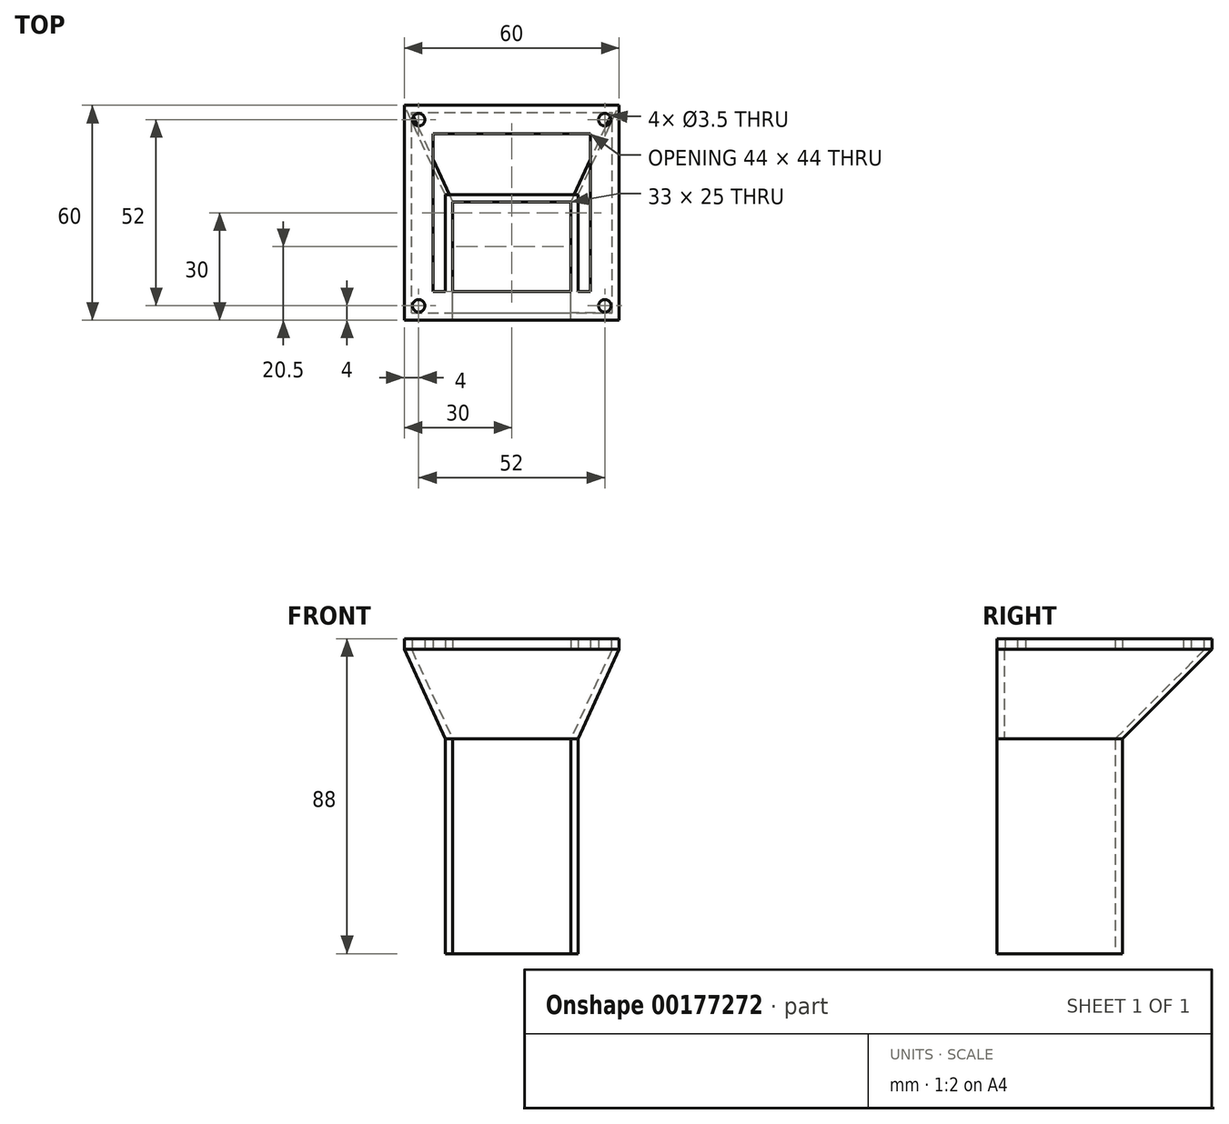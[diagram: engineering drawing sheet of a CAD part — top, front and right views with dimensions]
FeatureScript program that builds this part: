
annotation { "Feature Type Name" : "Feature", "Feature Type Description" : "" }
export const myFeature = defineFeature(function(context is Context, id is Id, definition is map)
    precondition{}
    {
        {
            var Q0;
            Q0=qCreatedBy(makeId("Top.planeOp"),FACE);
            var sketch = newSketch(context, id + "F0", { "sketchPlane" : qUnion([Q0])});
            skLineSegment(sketch, "E0.bottom", {"start": v(0, 0) * mm, "end": v(33, 0) * mm});
            skLineSegment(sketch, "E0.top", {"start": v(0, 33) * mm, "end": v(33, 33) * mm});
            skLineSegment(sketch, "E0.left", {"start": v(0, 0) * mm, "end": v(0, 33) * mm});
            skLineSegment(sketch, "E0.right", {"start": v(33, 0) * mm, "end": v(33, 33) * mm});
            skLineSegment(sketch, "E1.0", {"start": v(-2, 35) * mm, "end": v(35, 35) * mm});
            skLineSegment(sketch, "E1.1", {"start": v(-2, 0) * mm, "end": v(-2, 35) * mm});
            skLineSegment(sketch, "E1.3", {"start": v(35, 0) * mm, "end": v(35, 35) * mm});
            skLineSegment(sketch, "E2", {"start": v(33, 0) * mm, "end": v(35, 0) * mm});
            skLineSegment(sketch, "E3", {"start": v(0, 0) * mm, "end": v(-2, 0) * mm});
            skSolve(sketch);
        }
        {
            var Q0;
            Q0=makeQuery(id+"F0.imprint","IMPRINT",FACE,{"disambiguationData":[TD([[makeQuery(id+"F0.imprint","IMPRINT",EDGE,{"derivedFrom":sQuery(id+"F0.wireOp",EDGE,"E0.top")}),1.0]])]});
            extrude(context, id + "F1", {"entities" : qUnion([Q0]), "depth" : 60 * mm});
        }
        {
            var Q0;
            Q0=makeQuery(id+"F1.opExtrude","CAP_FACE",FACE,{"disambiguationData":[OSD([sQuery(id+"F0.wireOp",EDGE,"E0.top"),sQuery(id+"F0.wireOp",EDGE,"E0.left"),sQuery(id+"F0.wireOp",EDGE,"E0.right"),sQuery(id+"F0.wireOp",EDGE,"E1.0"),sQuery(id+"F0.wireOp",EDGE,"E1.1"),sQuery(id+"F0.wireOp",EDGE,"E1.3"),sQuery(id+"F0.wireOp",EDGE,"E2"),sQuery(id+"F0.wireOp",EDGE,"E3")])],"isStart":false});
            cPlane(context, id + "F2", {"entities" : qUnion([Q0]), "cplaneType" : CPlaneType.OFFSET, "offset" : 25 * mm, "width" : 150 * mm, "height" : 150 * mm});
        }
        {
            var Q0;
            Q0=qCreatedBy(id+"F2.planeOp",FACE);
            var sketch = newSketch(context, id + "F3", { "sketchPlane" : qUnion([Q0])});
            skLineSegment(sketch, "E4.0.0", {"start": v(0, 0) * mm, "end": v(0, 33) * mm});
            skLineSegment(sketch, "E4.0.1", {"start": v(0, 33) * mm, "end": v(33, 33) * mm});
            skLineSegment(sketch, "E4.0.2", {"start": v(33, 33) * mm, "end": v(33, 0) * mm});
            skLineSegment(sketch, "E4.0.3", {"start": v(33, 0) * mm, "end": v(35, 0) * mm});
            skLineSegment(sketch, "E4.0.4", {"start": v(35, 0) * mm, "end": v(35, 35) * mm});
            skLineSegment(sketch, "E4.0.5", {"start": v(35, 35) * mm, "end": v(-2, 35) * mm});
            skLineSegment(sketch, "E4.0.6", {"start": v(-2, 35) * mm, "end": v(-2, 0) * mm});
            skLineSegment(sketch, "E4.0.7", {"start": v(-2, 0) * mm, "end": v(0, 0) * mm});
            skLineSegment(sketch, "E5.bottom", {"start": v(-13.5, 0) * mm, "end": v(46.5, 0) * mm});
            skLineSegment(sketch, "E5.top", {"start": v(-13.5, 60) * mm, "end": v(46.5, 60) * mm});
            skLineSegment(sketch, "E5.left", {"start": v(-13.5, 0) * mm, "end": v(-13.5, 60) * mm});
            skLineSegment(sketch, "E5.right", {"start": v(46.5, 0) * mm, "end": v(46.5, 60) * mm});
            skLineSegment(sketch, "E6", {"start": v(16.5, 60.15) * mm, "end": v(16.5, -12.5) * mm, "construction": true});
            skPoint(sketch, "E6.startSnap0", {"position": v(16.5, 35) * mm});
            skPoint(sketch, "E6.endSnap0", {"position": v(16.5, 35) * mm});
            skLineSegment(sketch, "E7.0", {"start": v(-5.5, 52) * mm, "end": v(38.5, 52) * mm});
            skLineSegment(sketch, "E7.1", {"start": v(-5.5, 8) * mm, "end": v(-5.5, 52) * mm});
            skLineSegment(sketch, "E7.2", {"start": v(-5.5, 8) * mm, "end": v(38.5, 8) * mm});
            skLineSegment(sketch, "E7.3", {"start": v(38.5, 8) * mm, "end": v(38.5, 52) * mm});
            skCircle(sketch, "E8", {"center": v(-9.5, 56) * mm, "radius": 1.75 * mm});
            skCircle(sketch, "E9", {"center": v(-9.5, 4) * mm, "radius": 1.75 * mm});
            skCircle(sketch, "E10", {"center": v(42.5, 4) * mm, "radius": 1.75 * mm});
            skCircle(sketch, "E11", {"center": v(42.5, 56) * mm, "radius": 1.75 * mm});
            skLineSegment(sketch, "E12", {"start": v(-5.5, 8) * mm, "end": v(-5.5, 0) * mm});
            skLineSegment(sketch, "E13", {"start": v(38.5, 8) * mm, "end": v(38.5, 0) * mm});
            skSolve(sketch);
        }
        {
            var Q0;
            Q0=makeQuery(id+"F3.imprint","IMPRINT",FACE,{"disambiguationData":[TD([[makeQuery(id+"F3.imprint","IMPRINT",EDGE,{"derivedFrom":sQuery(id+"F3.wireOp",EDGE,"E5.top")}),-1.0]])]});
            var Q1;
            {var subQ5=sQuery(id+"F3.wireOp",EDGE,"E12");Q1=makeQuery(id+"F3.imprint","IMPRINT",FACE,{"disambiguationData":[TD([[makeQuery(id+"F3.imprint","IMPRINT",EDGE,{"derivedFrom":subQ5}),1.0]])]});}
            var Q2;
            {var subQ5=sQuery(id+"F3.wireOp",EDGE,"E13");Q2=makeQuery(id+"F3.imprint","IMPRINT",FACE,{"disambiguationData":[TD([[makeQuery(id+"F3.imprint","IMPRINT",EDGE,{"derivedFrom":subQ5}),-1.0]])]});}
            var Q3;
            {var subQ0=sQuery(id+"F3.wireOp",EDGE,"E5.bottom");var subQ1=sQuery(id+"F3.wireOp",EDGE,"E4.0.2");var subQ2=makeQuery(id+"F3.imprint","INTERSECT",VERTEX,{"derivedFrom":[subQ1,subQ0]});Q3=makeQuery(id+"F3.imprint","IMPRINT",FACE,{"disambiguationData":[TD([[makeQuery(id+"F3.imprint","IMPRINT",EDGE,{"disambiguationData":[TD([[subQ2,1.0]])],"derivedFrom":subQ1}),1.0]])]});}
            var Q4;
            {var subQ0=sQuery(id+"F3.wireOp",EDGE,"E5.bottom");var subQ1=sQuery(id+"F3.wireOp",EDGE,"E4.0.0");var subQ2=makeQuery(id+"F3.imprint","INTERSECT",VERTEX,{"derivedFrom":[subQ1,subQ0]});Q4=makeQuery(id+"F3.imprint","IMPRINT",FACE,{"disambiguationData":[TD([[makeQuery(id+"F3.imprint","IMPRINT",EDGE,{"disambiguationData":[TD([[subQ2,-1.0]])],"derivedFrom":subQ1}),1.0]])]});}
            var Q5;
            Q5=makeQuery(id+"F3.imprint","IMPRINT",FACE,{"disambiguationData":[TD([[makeQuery(id+"F3.imprint","IMPRINT",EDGE,{"derivedFrom":sQuery(id+"F3.wireOp",EDGE,"E7.0")}),1.0]])]});
            var Q6;
            {var subQ0=sQuery(id+"F3.wireOp",EDGE,"af95f293-ccdd-4cf6-88c4-fea35add42e6.1");var subQ1=sQuery(id+"F3.wireOp",EDGE,"E4.0.0");var subQ2=makeQuery(id+"F3.imprint","INTERSECT",VERTEX,{"derivedFrom":[subQ1,subQ0]});Q6=makeQuery(id+"F3.imprint","IMPRINT",FACE,{"disambiguationData":[TD([[makeQuery(id+"F3.imprint","IMPRINT",EDGE,{"disambiguationData":[TD([[subQ2,-1.0]])],"derivedFrom":subQ1}),1.0]])]});}
            var Q7;
            {var subQ0=sQuery(id+"F3.wireOp",EDGE,"E7.2");var subQ1=sQuery(id+"F3.wireOp",EDGE,"E4.0.2");var subQ2=makeQuery(id+"F3.imprint","INTERSECT",VERTEX,{"derivedFrom":[subQ1,subQ0]});Q7=makeQuery(id+"F3.imprint","IMPRINT",FACE,{"disambiguationData":[TD([[makeQuery(id+"F3.imprint","IMPRINT",EDGE,{"disambiguationData":[TD([[subQ2,-1.0]])],"derivedFrom":subQ1}),1.0]])]});}
            var Q8;
            {var subQ0=sQuery(id+"F3.wireOp",EDGE,"E5.bottom");var subQ1=sQuery(id+"F3.wireOp",EDGE,"E4.0.0");var subQ2=makeQuery(id+"F3.imprint","INTERSECT",VERTEX,{"derivedFrom":[subQ1,subQ0]});Q8=makeQuery(id+"F3.imprint","IMPRINT",FACE,{"disambiguationData":[TD([[makeQuery(id+"F3.imprint","IMPRINT",EDGE,{"disambiguationData":[TD([[subQ2,-1.0]])],"derivedFrom":subQ1}),-1.0]])]});}
            extrude(context, id + "F4", {"entities" : qUnion([Q0, Q1, Q2, Q3, Q4, Q5, Q6, Q7, Q8]), "depth" : 3 * mm});
        }
        {
            var Q0;
            Q0=makeQuery(id+"F3.imprint","IMPRINT",FACE,{"disambiguationData":[TD([[makeQuery(id+"F3.imprint","IMPRINT",EDGE,{"derivedFrom":sQuery(id+"F3.wireOp",EDGE,"E5.top")}),-1.0]])]});
            var sketch = newSketch(context, id + "F5", { "sketchPlane" : qUnion([Q0])});
            skLineSegment(sketch, "E14.0", {"start": v(-13.5, 0) * mm, "end": v(-13.5, 60) * mm});
            skLineSegment(sketch, "E15.0", {"start": v(-13.5, 60) * mm, "end": v(46.5, 60) * mm});
            skLineSegment(sketch, "E16.0", {"start": v(46.5, 0) * mm, "end": v(46.5, 60) * mm});
            skLineSegment(sketch, "E17.0", {"start": v(-13.5, 0) * mm, "end": v(46.5, 0) * mm});
            skSolve(sketch);
        }
        {
            var Q0;
            Q0=makeQuery(id+"F1.opExtrude","CAP_FACE",FACE,{"disambiguationData":[OSD([sQuery(id+"F0.wireOp",EDGE,"E0.top"),sQuery(id+"F0.wireOp",EDGE,"E0.left"),sQuery(id+"F0.wireOp",EDGE,"E0.right"),sQuery(id+"F0.wireOp",EDGE,"E1.0"),sQuery(id+"F0.wireOp",EDGE,"E1.1"),sQuery(id+"F0.wireOp",EDGE,"E1.3"),sQuery(id+"F0.wireOp",EDGE,"E2"),sQuery(id+"F0.wireOp",EDGE,"E3")])],"isStart":false});
            var sketch = newSketch(context, id + "F6", { "sketchPlane" : qUnion([Q0])});
            skLineSegment(sketch, "E18.0", {"start": v(-2, 0) * mm, "end": v(-2, 35) * mm});
            skLineSegment(sketch, "E19.0", {"start": v(-2, 35) * mm, "end": v(35, 35) * mm});
            skLineSegment(sketch, "E20.0", {"start": v(35, 0) * mm, "end": v(35, 35) * mm});
            skLineSegment(sketch, "E21", {"start": v(-2, 0) * mm, "end": v(35, 0) * mm});
            skSolve(sketch);
        }
        {
            var Q0;
            Q0 = qSketchRegion(id + "F6", true);
            var Q1;
            Q1 = qSketchRegion(id + "F5", true);
            loft(context, id + "F7", {"sheetProfilesArray" : [{ "sheetProfileEntities" : qUnion([Q0]) }, { "sheetProfileEntities" : qUnion([Q1]) }]});
        }
        {
            var Q0;
            Q0=makeQuery(id+"F4.opExtrude","CAP_FACE",FACE,{"disambiguationData":[OSD([sQuery(id+"F3.wireOp",EDGE,"E4.0.0"),sQuery(id+"F3.wireOp",EDGE,"E4.0.2"),sQuery(id+"F3.wireOp",EDGE,"E5.top"),sQuery(id+"F3.wireOp",EDGE,"E5.left"),sQuery(id+"F3.wireOp",EDGE,"E5.right"),sQuery(id+"F3.wireOp",EDGE,"E5.bottom"),sQuery(id+"F3.wireOp",EDGE,"E7.0"),sQuery(id+"F3.wireOp",EDGE,"E7.1"),sQuery(id+"F3.wireOp",EDGE,"E7.2"),sQuery(id+"F3.wireOp",EDGE,"E7.3"),sQuery(id+"F3.wireOp",EDGE,"E8"),sQuery(id+"F3.wireOp",EDGE,"E9"),sQuery(id+"F3.wireOp",EDGE,"E10"),sQuery(id+"F3.wireOp",EDGE,"E11")])],"isStart":true});
            cPlane(context, id + "F8", {"entities" : qUnion([Q0]), "cplaneType" : CPlaneType.OFFSET, "offset" : 0 * mm, "width" : 150 * mm, "height" : 150 * mm});
        }
        {
            var Q0;
            Q0=makeQuery(id+"F1.opExtrude","CAP_FACE",FACE,{"disambiguationData":[OSD([sQuery(id+"F0.wireOp",EDGE,"E0.top"),sQuery(id+"F0.wireOp",EDGE,"E0.left"),sQuery(id+"F0.wireOp",EDGE,"E0.right"),sQuery(id+"F0.wireOp",EDGE,"E1.0"),sQuery(id+"F0.wireOp",EDGE,"E1.1"),sQuery(id+"F0.wireOp",EDGE,"E1.3"),sQuery(id+"F0.wireOp",EDGE,"E2"),sQuery(id+"F0.wireOp",EDGE,"E3")])],"isStart":false});
            var sketch = newSketch(context, id + "F9", { "sketchPlane" : qUnion([Q0])});
            skLineSegment(sketch, "E22.0", {"start": v(0, 2) * mm, "end": v(0, 33) * mm});
            skLineSegment(sketch, "E23.0", {"start": v(0, 33) * mm, "end": v(33, 33) * mm});
            skLineSegment(sketch, "E24.0", {"start": v(33, 2) * mm, "end": v(33, 33) * mm});
            skLineSegment(sketch, "E25", {"start": v(0, 2) * mm, "end": v(2, 2) * mm});
            skLineSegment(sketch, "E26", {"start": v(2, 2) * mm, "end": v(4, 2) * mm});
            skLineSegment(sketch, "E27", {"start": v(4, 2) * mm, "end": v(29, 2) * mm});
            skLineSegment(sketch, "E28", {"start": v(29, 2) * mm, "end": v(31, 2) * mm});
            skLineSegment(sketch, "E29", {"start": v(31, 2) * mm, "end": v(33, 2) * mm});
            skPoint(sketch, "E30.start.orphan", {"position": v(0, 0) * mm});
            skPoint(sketch, "E31.orphan", {"position": v(33, 0) * mm});
            skSolve(sketch);
        }
        {
            var Q0;
            Q0=qCreatedBy(id+"F8.planeOp",FACE);
            var sketch = newSketch(context, id + "F10", { "sketchPlane" : qUnion([Q0])});
            skLineSegment(sketch, "E32.0", {"start": v(-11.5, -2) * mm, "end": v(-11.5, -58) * mm});
            skLineSegment(sketch, "E33.0", {"start": v(-11.5, -58) * mm, "end": v(44.5, -58) * mm});
            skLineSegment(sketch, "E34.0", {"start": v(44.5, -2) * mm, "end": v(44.5, -58) * mm});
            skLineSegment(sketch, "E35", {"start": v(-11.5, -2) * mm, "end": v(44.5, -2) * mm});
            skLineSegment(sketch, "E36.0", {"start": v(-13.5, 0) * mm, "end": v(-13.5, -60) * mm, "construction": true});
            skLineSegment(sketch, "E37.0", {"start": v(-13.5, 0) * mm, "end": v(46.5, 0) * mm, "construction": true});
            skLineSegment(sketch, "E38.0", {"start": v(46.5, 0) * mm, "end": v(46.5, -60) * mm, "construction": true});
            skLineSegment(sketch, "E39.0", {"start": v(-13.5, -60) * mm, "end": v(46.5, -60) * mm, "construction": true});
            skSolve(sketch);
        }
        {
            var Q0;
            Q0=makeQuery(id+"F10.imprint","IMPRINT",FACE,{"disambiguationData":[TD([[makeQuery(id+"F10.imprint","IMPRINT",EDGE,{"derivedFrom":sQuery(id+"F10.wireOp",EDGE,"E32.0")}),1.0]])]});
            var Q1;
            Q1=makeQuery(id+"F9.imprint","IMPRINT",FACE,{"disambiguationData":[TD([[makeQuery(id+"F9.imprint","IMPRINT",EDGE,{"derivedFrom":sQuery(id+"F9.wireOp",EDGE,"E22.0")}),-1.0]])]});
            var Q2;
            Q2=sQuery(id+"F9.wireOp",VERTEX,"E24.0.start");
            var Q3;
            Q3=sQuery(id+"F10.wireOp",VERTEX,"E35.end");
            loft(context, id + "F11", {"sheetProfilesArray" : [{ "sheetProfileEntities" : qUnion([Q0]) }, { "sheetProfileEntities" : qUnion([Q1]) }], "matchConnections" : true, "connections" : [{ "connectionEntities" : qUnion([Q2, Q3]), "connectionEdgeQueries" : qUnion([]), "connectionEdgeParameters" : [] }]});
        }
        {
            var Q0;
            Q0=makeQuery(id+"F11.opLoft","SWEPT_FACE",FACE,{"disambiguationData":[OSD([sQuery(id+"F0.wireOp",EDGE,"E0.right"),sQuery(id+"F9.wireOp",EDGE,"E24.0"),sQuery(id+"F9.wireOp",EDGE,"E28"),sQuery(id+"F9.wireOp",EDGE,"E29"),sQuery(id+"F10.wireOp",EDGE,"E34.0"),sQuery(id+"F10.wireOp",EDGE,"E35")])]});
            var sketch = newSketch(context, id + "F12", { "sketchPlane" : qUnion([Q0])});
            skLineSegment(sketch, "E40", {"start": v(33, 60) * mm, "end": v(33, 85) * mm});
            skLineSegment(sketch, "E41", {"start": v(0, 60) * mm, "end": v(0, 85) * mm});
            skLineSegment(sketch, "E42", {"start": v(0, 85) * mm, "end": v(33, 85) * mm});
            skLineSegment(sketch, "E43", {"start": v(33, 60) * mm, "end": v(0, 60) * mm});
            skSolve(sketch);
        }
        {
            var Q0;
            Q0=makeQuery(id+"F11.opLoft","SWEPT_BODY",BODY,{"disambiguationData":[OSD([makeQuery(id+"F9.imprint","IMPRINT",FACE,{"disambiguationData":[TD([[makeQuery(id+"F9.imprint","IMPRINT",EDGE,{"derivedFrom":sQuery(id+"F9.wireOp",EDGE,"E22.0")}),-1.0]])]}),makeQuery(id+"F10.imprint","IMPRINT",FACE,{"disambiguationData":[TD([[makeQuery(id+"F10.imprint","IMPRINT",EDGE,{"derivedFrom":sQuery(id+"F10.wireOp",EDGE,"2033aaa8-1e85-4015-bb98-e518b16fd1b1.0")}),-1.0]])]})])]});
            var Q1;
            {var subQ3=sQuery(id+"F6.wireOp",EDGE,"E18.0");Q1=makeQuery(id+"F7.opLoft","SWEPT_BODY",BODY,{"disambiguationData":[OSD([makeQuery(id+"F5.imprint","IMPRINT",FACE,{"disambiguationData":[TD([[makeQuery(id+"F5.imprint","IMPRINT",EDGE,{"derivedFrom":makeQuery(id+"F3.imprint","IMPRINT",EDGE,{"derivedFrom":sQuery(id+"F3.wireOp",EDGE,"E7.0")})}),-1.0]])]}),makeQuery(id+"F6.imprint","IMPRINT",FACE,{"disambiguationData":[TD([[makeQuery(id+"F6.imprint","IMPRINT",EDGE,{"derivedFrom":subQ3}),-1.0]])]})])]});}
            booleanBodies(context, id + "F13", {"operationType" : BooleanOperationType.SUBTRACTION, "tools" : qUnion([Q0]), "targets" : qUnion([Q1])});
        }
    });
